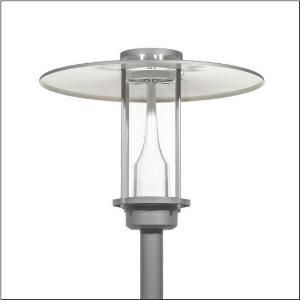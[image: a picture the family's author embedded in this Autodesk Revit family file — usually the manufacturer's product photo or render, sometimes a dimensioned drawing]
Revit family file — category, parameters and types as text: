
# Revit family: city-light_plus_iq___p1_0a_5xa5275bf14hp_a9e6
name_source: partatom
category: Lighting Fixtures
units: mm (PartAtom-declared; Revit-internal decimal feet)

## family parameters
Cut with Voids When Loaded = No
Host = Face
Light Source = No
Part Type = Normal
Room Calculation Point = No
Round Connector Dimension = Use Diameter
Shared = No

## types (1)
- --- (1 x LED, 3710 lm, 33.6 W, 2200K)
    Apparent Load = 34 VA
    CIE Flux Codes = 30 60 90 96 100
    Color Rendering = 70
    Color Temperature = 2200K
    Default Elevation = 1800 mm
    Description = City-Light Plus iQ, mast luminaire, Module 540 iQ-SR, primary light control with 3 zone facetted reflector, of plastic, silver coated, highly specular, structured, primary optical cover: cover, of PMMA, transparent, light distribution: P1.0a, light emission: direct distribution, primary light characteristic: strongly asymmetric, installation type: post-top, LED, High Power LED, rated luminous flux: 3.710lm, luminous efficacy: 110lm/W, light colour: 722, colour temperature: 2200K, control gear: ECG iQ, control: presetting dimming logarithmic, Street-Remote, Auto-Match, Temp-Guard, Lumen-Switch, Night-Set, Smart-Wire, Light-Fading, Desk-Remote (wireless, voltage-free reading and setting of iQ features in the workshop via application-optimized NFC function/RFID function), optimised constant luminous flux control (CLO 2.0), with terminal, 6-pole, max. 2.5mm², mains connection: 230..240V, AC, 50/60Hz, start of lifetime: 34W, end of service life: 36W, reduction: 15W, luminaire housing, upper part, of glass-fibre reinforced polyester, coated, Siteco® metallic grey (DB 702S), diameter: 750mm, height: 590mm, spigot size: d x l = 76 x 70mm (post-top) | with reducer (optional accessory) 60 x 70mm, post-top mast mounting element, of diecast aluminium, coated, Siteco® metallic grey (DB 702S), Module 540 iQ-SR, traffic white (RAL 9016), equipment: Power, protection rating (complete): IP65, insulation class (complete): insulation class II (safety insulation), certification: CE, ENEC, VDE, packaging unit: 1 piece

Light Distribution: P1.0a
    Height = 590 mm
    Lamp = 1 x LED
    Lamp Light Flux = 3710 lm
    Lamp Power = 33.6 W
    Lamp count = 1
    Length = 750 mm
    Luminous efficacy = 110 lm/W
    Manufacturer = Siteco
    ModVariant = No
    Model = 5XA5275BF14HP
    Number of Poles = 1
    OnlyDefault = Yes
    Power Factor = 1
    Product Name = City-Light Plus iQ | P1.0a
    Product group = mast luminaire | pylon top
    ProductGroupID = 6100
    Protection Class = Protection class II
    Protection Degree = IP 65
    RLX_Detail_Level = 1
    RLX_Emergency_Light_Flux = 0 lm
    RLX_Emergency_Type = 0
    RLX_Emergency_Type_DB = No
    RlxData = <blob elided: 52529 chars, md5=b84ffa81>
    Socket = socket
    Standby Power = 0 W
    System Light Flux = 3710 lm
    System Power = 34 W
    Type Comments = factory setting: luminous flux: 100 % | dim-lin: 254 | 695 mA
    Type Image = l_1006456.jpg
    URL = http://relux.com
    VarID = @adj_146417
    Voltage = 0 V
    Weight = 0.00 kg
    Width = 0 mm  [stored 0 ft]

note: [stored X ft] marks values corroborated as IEEE doubles in the binary element streams (Revit-internal decimal feet)

## geometry (parser evidence)
native form markers: Blend x4, Sweep x11
no freeform markers — native parametric forms only
